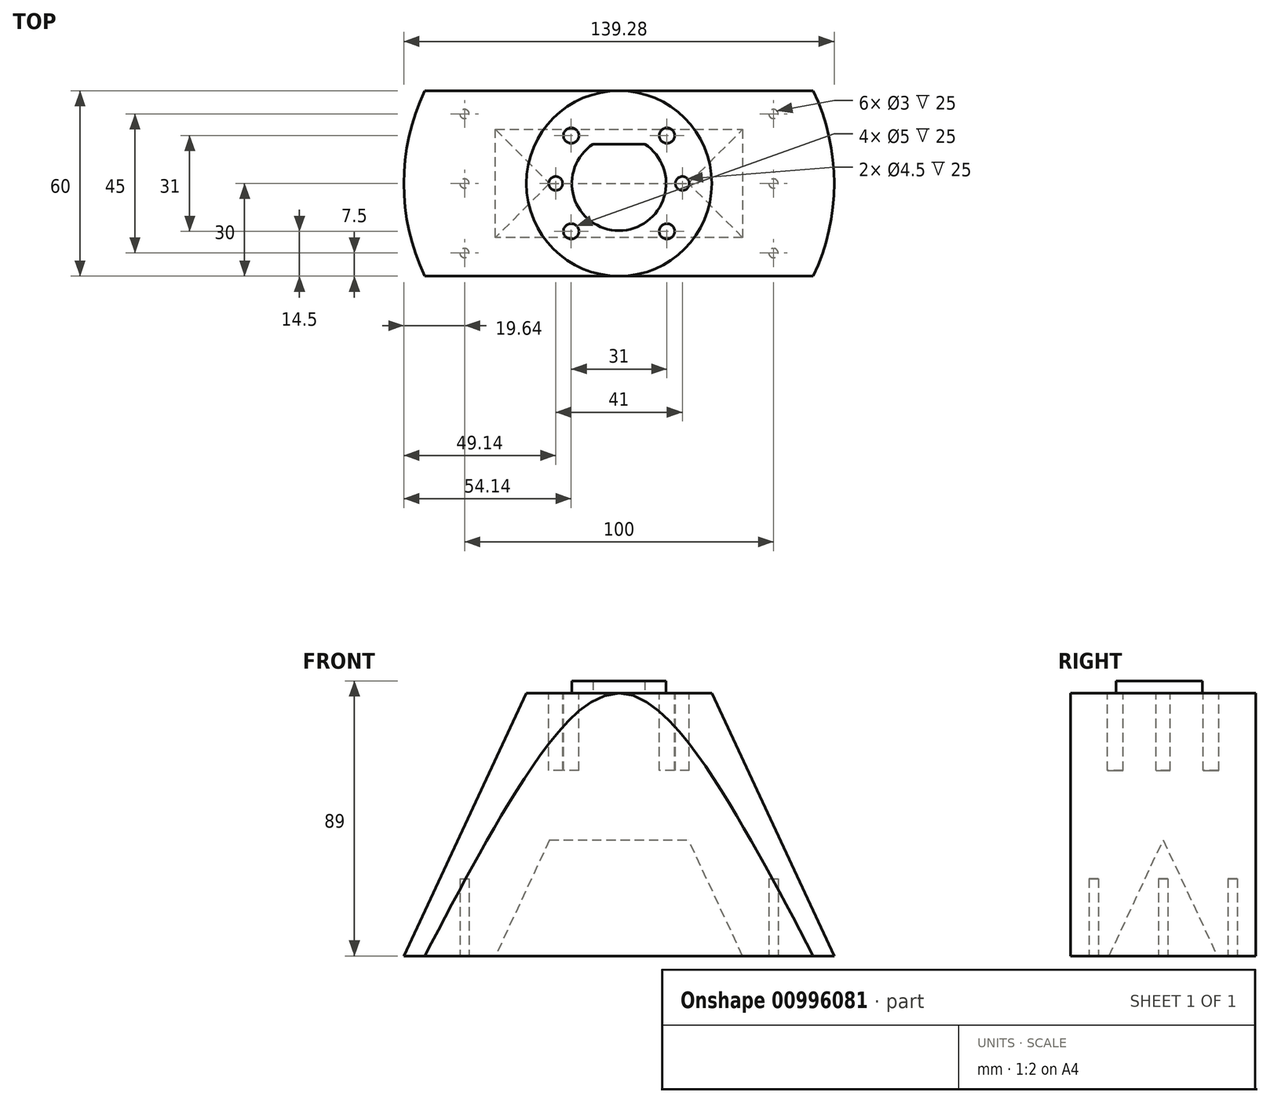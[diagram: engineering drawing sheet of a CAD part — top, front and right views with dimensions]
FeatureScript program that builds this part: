
annotation { "Feature Type Name" : "Feature", "Feature Type Description" : "" }
export const myFeature = defineFeature(function(context is Context, id is Id, definition is map)
    precondition{}
    {
        {
            var Q0;
            Q0=qCreatedBy(makeId("Top.planeOp"),FACE);
            var sketch = newSketch(context, id + "F0", { "sketchPlane" : qUnion([Q0])});
            skCircle(sketch, "E0", {"center": v(0, 0) * mm, "radius": 30 * mm});
            skSolve(sketch);
        }
        {
            var Q0;
            Q0 = qSketchRegion(id + "F0", true);
            extrude(context, id + "F1", {"entities" : qUnion([Q0]), "oppositeDirection" : true, "depth" : 85 * mm, "offsetDistance" : 25 * mm, "hasDraft" : true, "draftAngle" : 25 * degree});
        }
        {
            var Q0;
            Q0=makeQuery(id+"F1.opExtrude","CAP_FACE",FACE,{"disambiguationData":[OSD([sQuery(id+"F0.wireOp",EDGE,"E0")])],"isStart":true});
            var sketch = newSketch(context, id + "F2", { "sketchPlane" : qUnion([Q0])});
            skLineSegment(sketch, "E1.bottom", {"start": v(-73.2, -30) * mm, "end": v(72.82, -30) * mm});
            skLineSegment(sketch, "E1.top", {"start": v(-73.2, -72.85) * mm, "end": v(72.82, -72.85) * mm});
            skLineSegment(sketch, "E1.left", {"start": v(-73.2, -30) * mm, "end": v(-73.2, -72.85) * mm});
            skLineSegment(sketch, "E1.right", {"start": v(72.82, -30) * mm, "end": v(72.82, -72.85) * mm});
            skLineSegment(sketch, "E2.bottom", {"start": v(-83.7, 73.1) * mm, "end": v(116.3, 73.1) * mm});
            skLineSegment(sketch, "E2.top", {"start": v(-83.7, 30) * mm, "end": v(116.3, 30) * mm});
            skLineSegment(sketch, "E2.left", {"start": v(-83.7, 73.1) * mm, "end": v(-83.7, 30) * mm});
            skLineSegment(sketch, "E2.right", {"start": v(116.3, 73.1) * mm, "end": v(116.3, 30) * mm});
            skSolve(sketch);
        }
        {
            var Q0;
            Q0 = qSketchRegion(id + "F2", true);
            extrude(context, id + "F3", {"entities" : qUnion([Q0]), "operationType" : NewBodyOperationType.REMOVE, "oppositeDirection" : true, "depth" : 90 * mm, "offsetDistance" : 25 * mm});
        }
        {
            var Q0;
            Q0=makeQuery(id+"F1.opExtrude","CAP_FACE",FACE,{"disambiguationData":[OSD([sQuery(id+"F0.wireOp",EDGE,"E0")])],"isStart":true});
            var sketch = newSketch(context, id + "F4", { "sketchPlane" : qUnion([Q0])});
            skArc(sketch, "E3", {"start": v(-8.37, 12.75) * mm, "mid": v(0, -15.25) * mm, "end": v(8.37, 12.75) * mm});
            skLineSegment(sketch, "E4", {"start": v(-8.37, 12.75) * mm, "end": v(8.37, 12.75) * mm});
            skPoint(sketch, "E5.orphan", {"position": v(21.18, 12.75) * mm});
            skSolve(sketch);
        }
        {
            var Q0;
            Q0 = qSketchRegion(id + "F4", true);
            extrude(context, id + "F5", {"entities" : qUnion([Q0]), "operationType" : NewBodyOperationType.ADD, "depth" : 4 * mm, "offsetDistance" : 25 * mm});
        }
        {
            var Q0;
            Q0=makeQuery(id+"F1.opExtrude","CAP_FACE",FACE,{"disambiguationData":[OSD([sQuery(id+"F0.wireOp",EDGE,"E0")])],"isStart":true});
            var sketch = newSketch(context, id + "F6", { "sketchPlane" : qUnion([Q0])});
            skLineSegment(sketch, "E6.bottom", {"start": v(15.5, 15.5) * mm, "end": v(-15.5, 15.5) * mm, "construction": true});
            skLineSegment(sketch, "E6.top", {"start": v(15.5, -15.5) * mm, "end": v(-15.5, -15.5) * mm, "construction": true});
            skLineSegment(sketch, "E6.left", {"start": v(15.5, 15.5) * mm, "end": v(15.5, -15.5) * mm, "construction": true});
            skLineSegment(sketch, "E6.right", {"start": v(-15.5, 15.5) * mm, "end": v(-15.5, -15.5) * mm, "construction": true});
            skPoint(sketch, "E6.middle", {"position": v(0, 0) * mm});
            skCircle(sketch, "E7", {"center": v(15.5, 15.5) * mm, "radius": 2.5 * mm});
            skCircle(sketch, "E8", {"center": v(-15.5, 15.5) * mm, "radius": 2.5 * mm});
            skCircle(sketch, "E9", {"center": v(-15.5, -15.5) * mm, "radius": 2.5 * mm});
            skCircle(sketch, "E10", {"center": v(15.5, -15.5) * mm, "radius": 2.5 * mm});
            skLineSegment(sketch, "E11", {"start": v(-20.5, 0) * mm, "end": v(20.5, 0) * mm, "construction": true});
            skCircle(sketch, "E12", {"center": v(-20.5, 0) * mm, "radius": 2.25 * mm});
            skCircle(sketch, "E13", {"center": v(20.5, 0) * mm, "radius": 2.25 * mm});
            skSolve(sketch);
        }
        {
            var Q0;
            Q0 = qSketchRegion(id + "F6", true);
            extrude(context, id + "F7", {"entities" : qUnion([Q0]), "operationType" : NewBodyOperationType.REMOVE, "oppositeDirection" : true, "depth" : 25 * mm, "offsetDistance" : 25 * mm});
        }
        {
            var Q0;
            Q0=makeQuery(id+"F1.opExtrude","CAP_FACE",FACE,{"disambiguationData":[OSD([sQuery(id+"F0.wireOp",EDGE,"E0")])],"isStart":false});
            var sketch = newSketch(context, id + "F8", { "sketchPlane" : qUnion([Q0])});
            skLineSegment(sketch, "E14.bottom", {"start": v(40, 17.5) * mm, "end": v(-40, 17.5) * mm});
            skLineSegment(sketch, "E14.top", {"start": v(40, -17.5) * mm, "end": v(-40, -17.5) * mm});
            skLineSegment(sketch, "E14.left", {"start": v(40, 17.5) * mm, "end": v(40, -17.5) * mm});
            skLineSegment(sketch, "E14.right", {"start": v(-40, 17.5) * mm, "end": v(-40, -17.5) * mm});
            skPoint(sketch, "E14.middle", {"position": v(0, 0) * mm});
            skLineSegment(sketch, "E15.bottom", {"start": v(50, 22.5) * mm, "end": v(-50, 22.5) * mm, "construction": true});
            skLineSegment(sketch, "E15.top", {"start": v(50, -22.5) * mm, "end": v(-50, -22.5) * mm, "construction": true});
            skLineSegment(sketch, "E15.left", {"start": v(50, 22.5) * mm, "end": v(50, -22.5) * mm, "construction": true});
            skLineSegment(sketch, "E15.right", {"start": v(-50, 22.5) * mm, "end": v(-50, -22.5) * mm, "construction": true});
            skCircle(sketch, "E16", {"center": v(-50, 22.5) * mm, "radius": 1.5 * mm});
            skCircle(sketch, "E17", {"center": v(50, 22.5) * mm, "radius": 1.5 * mm});
            skCircle(sketch, "E18", {"center": v(50, -22.5) * mm, "radius": 1.5 * mm});
            skCircle(sketch, "E19", {"center": v(-50, -22.5) * mm, "radius": 1.5 * mm});
            skCircle(sketch, "E20", {"center": v(-50, 0) * mm, "radius": 1.5 * mm});
            skCircle(sketch, "E21", {"center": v(50, 0) * mm, "radius": 1.5 * mm});
            skSolve(sketch);
        }
        {
            var Q0;
            Q0=makeQuery(id+"F8.imprint","IMPRINT",FACE,{"disambiguationData":[TD([[makeQuery(id+"F8.imprint","IMPRINT",EDGE,{"derivedFrom":sQuery(id+"F8.wireOp",EDGE,"E16")}),1.0]])]});
            var Q1;
            Q1=makeQuery(id+"F8.imprint","IMPRINT",FACE,{"disambiguationData":[TD([[makeQuery(id+"F8.imprint","IMPRINT",EDGE,{"derivedFrom":sQuery(id+"F8.wireOp",EDGE,"E20")}),1.0]])]});
            var Q2;
            Q2=makeQuery(id+"F8.imprint","IMPRINT",FACE,{"disambiguationData":[TD([[makeQuery(id+"F8.imprint","IMPRINT",EDGE,{"derivedFrom":sQuery(id+"F8.wireOp",EDGE,"E19")}),1.0]])]});
            var Q3;
            Q3=makeQuery(id+"F8.imprint","IMPRINT",FACE,{"disambiguationData":[TD([[makeQuery(id+"F8.imprint","IMPRINT",EDGE,{"derivedFrom":sQuery(id+"F8.wireOp",EDGE,"E18")}),1.0]])]});
            var Q4;
            Q4=makeQuery(id+"F8.imprint","IMPRINT",FACE,{"disambiguationData":[TD([[makeQuery(id+"F8.imprint","IMPRINT",EDGE,{"derivedFrom":sQuery(id+"F8.wireOp",EDGE,"E21")}),1.0]])]});
            var Q5;
            Q5=makeQuery(id+"F8.imprint","IMPRINT",FACE,{"disambiguationData":[TD([[makeQuery(id+"F8.imprint","IMPRINT",EDGE,{"derivedFrom":sQuery(id+"F8.wireOp",EDGE,"E17")}),1.0]])]});
            extrude(context, id + "F9", {"entities" : qUnion([Q0, Q1, Q2, Q3, Q4, Q5]), "operationType" : NewBodyOperationType.REMOVE, "oppositeDirection" : true, "depth" : 25 * mm, "offsetDistance" : 25 * mm});
        }
        {
            var Q0;
            Q0=makeQuery(id+"F8.imprint","IMPRINT",FACE,{"disambiguationData":[TD([[makeQuery(id+"F8.imprint","IMPRINT",EDGE,{"derivedFrom":sQuery(id+"F8.wireOp",EDGE,"E14.bottom")}),1.0]])]});
            extrude(context, id + "F10", {"entities" : qUnion([Q0]), "operationType" : NewBodyOperationType.REMOVE, "oppositeDirection" : true, "depth" : 50 * mm, "offsetDistance" : 25 * mm, "hasDraft" : true, "draftAngle" : 25 * degree, "draftPullDirection" : true});
        }
    });
